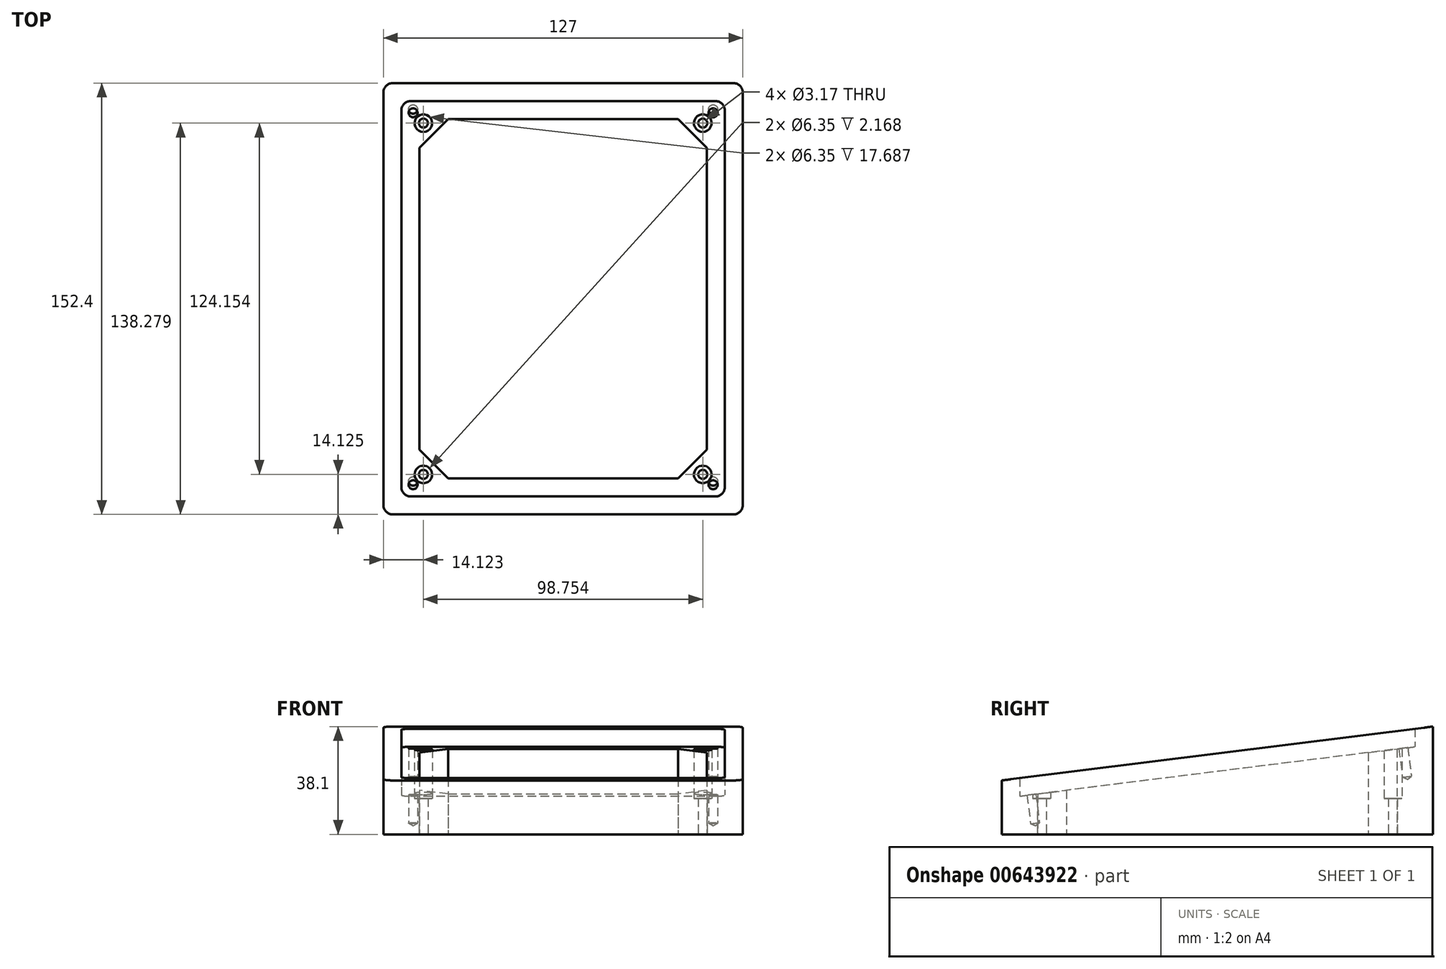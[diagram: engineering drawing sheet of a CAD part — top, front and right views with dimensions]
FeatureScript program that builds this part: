
annotation { "Feature Type Name" : "Feature", "Feature Type Description" : "" }
export const myFeature = defineFeature(function(context is Context, id is Id, definition is map)
    precondition{}
    {
        {
            var Q0;
            Q0=qCreatedBy(makeId("Top.planeOp"),FACE);
            var sketch = newSketch(context, id + "F0", { "sketchPlane" : qUnion([Q0])});
            skLineSegment(sketch, "E0.bottom", {"start": v(-63.5, 77.08) * mm, "end": v(63.5, 77.08) * mm});
            skLineSegment(sketch, "E0.top", {"start": v(-63.5, -75.32) * mm, "end": v(63.5, -75.32) * mm});
            skLineSegment(sketch, "E0.left", {"start": v(-63.5, 77.08) * mm, "end": v(-63.5, -75.32) * mm});
            skLineSegment(sketch, "E0.right", {"start": v(63.5, 77.08) * mm, "end": v(63.5, -75.32) * mm});
            skPoint(sketch, "E0.middle", {"position": v(0, 0.88) * mm});
            skLineSegment(sketch, "E1.bottom", {"start": v(-53.98, 70.73) * mm, "end": v(53.97, 70.73) * mm});
            skLineSegment(sketch, "E1.top", {"start": v(-53.98, -68.97) * mm, "end": v(53.97, -68.97) * mm});
            skLineSegment(sketch, "E1.left", {"start": v(-57.15, 67.56) * mm, "end": v(-57.15, -65.8) * mm});
            skLineSegment(sketch, "E1.right", {"start": v(57.15, 67.56) * mm, "end": v(57.15, -65.8) * mm});
            skLineSegment(sketch, "E2.bottom", {"start": v(-47.63, 64.38) * mm, "end": v(47.62, 64.38) * mm});
            skLineSegment(sketch, "E2.top", {"start": v(-47.63, -62.62) * mm, "end": v(48.25, -62.62) * mm});
            skLineSegment(sketch, "E2.left", {"start": v(-50.8, 61.2) * mm, "end": v(-50.8, -59.44) * mm});
            skLineSegment(sketch, "E2.right", {"start": v(50.8, 61.2) * mm, "end": v(50.8, -60.07) * mm});
            skPoint(sketch, "E3.visualSharp", {"position": v(-57.15, 70.73) * mm});
            skArc(sketch, "E3.filletArc", {"start": v(-53.98, 70.73) * mm, "mid": v(-56.22, 69.8) * mm, "end": v(-57.15, 67.56) * mm});
            skPoint(sketch, "E4.visualSharp", {"position": v(57.15, 70.73) * mm});
            skArc(sketch, "E4.filletArc", {"start": v(57.15, 67.56) * mm, "mid": v(56.22, 69.8) * mm, "end": v(53.97, 70.73) * mm});
            skPoint(sketch, "E5.visualSharp", {"position": v(57.15, -68.97) * mm});
            skArc(sketch, "E5.filletArc", {"start": v(53.97, -68.97) * mm, "mid": v(56.22, -68.04) * mm, "end": v(57.15, -65.8) * mm});
            skPoint(sketch, "E6.visualSharp", {"position": v(-57.15, -68.97) * mm});
            skArc(sketch, "E6.filletArc", {"start": v(-57.15, -65.8) * mm, "mid": v(-56.22, -68.04) * mm, "end": v(-53.98, -68.97) * mm});
            skPoint(sketch, "E7.visualSharp", {"position": v(50.8, 64.38) * mm});
            skArc(sketch, "E7.filletArc", {"start": v(50.8, 61.2) * mm, "mid": v(49.87, 63.45) * mm, "end": v(47.62, 64.38) * mm});
            skPoint(sketch, "E8.visualSharp", {"position": v(50.8, -62.62) * mm});
            skArc(sketch, "E8.filletArc", {"start": v(48.25, -62.62) * mm, "mid": v(50.05, -61.87) * mm, "end": v(50.8, -60.07) * mm});
            skPoint(sketch, "E9.visualSharp", {"position": v(-50.8, -62.62) * mm});
            skArc(sketch, "E9.filletArc", {"start": v(-50.8, -59.44) * mm, "mid": v(-49.87, -61.69) * mm, "end": v(-47.63, -62.62) * mm});
            skArc(sketch, "E10.filletArc", {"start": v(-47.63, 64.38) * mm, "mid": v(-49.87, 63.45) * mm, "end": v(-50.8, 61.2) * mm});
            skPoint(sketch, "E11.visualSharp", {"position": v(-63.5, 77.08) * mm});
            skLineSegment(sketch, "E11.filletArc", {"start": v(-63.5, 77.08) * mm, "end": v(-63.5, 77.08) * mm});
            skPoint(sketch, "E12.visualSharp", {"position": v(63.5, 77.08) * mm});
            skLineSegment(sketch, "E12.filletArc", {"start": v(63.5, 77.08) * mm, "end": v(63.5, 77.08) * mm});
            skPoint(sketch, "E13.visualSharp", {"position": v(63.5, -75.32) * mm});
            skLineSegment(sketch, "E13.filletArc", {"start": v(63.5, -75.32) * mm, "end": v(63.5, -75.32) * mm});
            skPoint(sketch, "E14.visualSharp", {"position": v(-63.5, -75.32) * mm});
            skLineSegment(sketch, "E14.filletArc", {"start": v(-63.5, -75.32) * mm, "end": v(-63.5, -75.32) * mm});
            skPoint(sketch, "E15", {"position": v(15.87, 64.38) * mm});
            skPoint(sketch, "E16", {"position": v(15.87, 77.08) * mm});
            skPoint(sketch, "E17", {"position": v(15.87, -62.62) * mm});
            skPoint(sketch, "E18", {"position": v(15.87, -75.32) * mm});
            skPoint(sketch, "E19", {"position": v(-15.88, 77.08) * mm});
            skPoint(sketch, "E20", {"position": v(-15.88, 64.38) * mm});
            skPoint(sketch, "E21", {"position": v(-15.88, -62.62) * mm});
            skPoint(sketch, "E22", {"position": v(-15.88, -75.32) * mm});
            skPoint(sketch, "E23", {"position": v(0, 77.08) * mm});
            skPoint(sketch, "E24", {"position": v(0, -75.32) * mm});
            skPoint(sketch, "E25", {"position": v(-63.5, 0.88) * mm});
            skPoint(sketch, "E26", {"position": v(63.5, 0.88) * mm});
            skPoint(sketch, "E27", {"position": v(63.5, 16.76) * mm});
            skPoint(sketch, "E28", {"position": v(50.8, 16.76) * mm});
            skPoint(sketch, "E29", {"position": v(-50.8, 16.76) * mm});
            skPoint(sketch, "E30", {"position": v(-63.5, 16.76) * mm});
            skPoint(sketch, "E31", {"position": v(63.5, -15) * mm});
            skPoint(sketch, "E32", {"position": v(50.8, -15) * mm});
            skPoint(sketch, "E33", {"position": v(-50.8, -15) * mm});
            skPoint(sketch, "E34", {"position": v(-63.5, -15) * mm});
            skPoint(sketch, "E35", {"position": v(40.64, 64.38) * mm});
            skPoint(sketch, "E36", {"position": v(40.64, -62.62) * mm});
            skPoint(sketch, "E37", {"position": v(-40.64, 64.38) * mm});
            skPoint(sketch, "E38", {"position": v(-40.64, -62.62) * mm});
            skPoint(sketch, "E39", {"position": v(-50.8, -52.46) * mm});
            skPoint(sketch, "E40", {"position": v(50.8, -52.46) * mm});
            skPoint(sketch, "E41", {"position": v(50.8, 54.22) * mm});
            skPoint(sketch, "E42", {"position": v(-50.8, 54.22) * mm});
            skLineSegment(sketch, "E43", {"start": v(-50.8, 54.22) * mm, "end": v(-40.64, 64.38) * mm});
            skLineSegment(sketch, "E44", {"start": v(40.64, 64.38) * mm, "end": v(50.8, 54.22) * mm});
            skLineSegment(sketch, "E45", {"start": v(50.8, -52.46) * mm, "end": v(40.64, -62.62) * mm});
            skLineSegment(sketch, "E46", {"start": v(-40.64, -62.62) * mm, "end": v(-50.8, -52.46) * mm});
            skPoint(sketch, "E47", {"position": v(-45.72, 59.3) * mm});
            skPoint(sketch, "E48", {"position": v(45.72, 59.3) * mm});
            skPoint(sketch, "E49", {"position": v(45.72, -57.54) * mm});
            skPoint(sketch, "E50", {"position": v(-45.72, -57.54) * mm});
            skPoint(sketch, "E51", {"position": v(30.16, 77.08) * mm});
            skPoint(sketch, "E52", {"position": v(30.16, 64.38) * mm});
            skPoint(sketch, "E53", {"position": v(30.16, -62.62) * mm});
            skPoint(sketch, "E54", {"position": v(30.16, -75.32) * mm});
            skPoint(sketch, "E55", {"position": v(-30.16, 77.08) * mm});
            skPoint(sketch, "E56", {"position": v(-30.16, 64.38) * mm});
            skPoint(sketch, "E57", {"position": v(-30.16, -62.62) * mm});
            skPoint(sketch, "E58", {"position": v(-30.16, -75.32) * mm});
            skPoint(sketch, "E59", {"position": v(63.5, 37.4) * mm});
            skPoint(sketch, "E60", {"position": v(50.8, 37.4) * mm});
            skPoint(sketch, "E61", {"position": v(-50.8, 37.4) * mm});
            skPoint(sketch, "E62", {"position": v(-63.5, 37.4) * mm});
            skPoint(sketch, "E63", {"position": v(63.5, -35.63) * mm});
            skPoint(sketch, "E64", {"position": v(50.8, -35.63) * mm});
            skPoint(sketch, "E65", {"position": v(-50.8, -35.63) * mm});
            skPoint(sketch, "E66", {"position": v(-63.5, -35.63) * mm});
            skPoint(sketch, "E67", {"position": v(-36.51, 77.08) * mm});
            skPoint(sketch, "E68", {"position": v(-36.51, 64.38) * mm});
            skPoint(sketch, "E69", {"position": v(-36.51, -62.62) * mm});
            skPoint(sketch, "E70", {"position": v(-36.51, -75.32) * mm});
            skPoint(sketch, "E71", {"position": v(36.51, 77.08) * mm});
            skPoint(sketch, "E72", {"position": v(36.51, 64.38) * mm});
            skPoint(sketch, "E73", {"position": v(36.51, -62.62) * mm});
            skPoint(sketch, "E74", {"position": v(36.51, -75.32) * mm});
            skPoint(sketch, "E75", {"position": v(-23.81, 77.08) * mm});
            skPoint(sketch, "E76", {"position": v(-23.81, 64.38) * mm});
            skPoint(sketch, "E77", {"position": v(23.81, 77.08) * mm});
            skPoint(sketch, "E78", {"position": v(23.81, 64.38) * mm});
            skPoint(sketch, "E79", {"position": v(23.81, -62.62) * mm});
            skPoint(sketch, "E80", {"position": v(23.81, -75.32) * mm});
            skPoint(sketch, "E81", {"position": v(-23.81, -62.62) * mm});
            skPoint(sketch, "E82", {"position": v(-23.81, -75.32) * mm});
            skPoint(sketch, "E83", {"position": v(-63.5, 43.74) * mm});
            skPoint(sketch, "E84", {"position": v(-50.8, 43.74) * mm});
            skPoint(sketch, "E85", {"position": v(50.8, 43.74) * mm});
            skPoint(sketch, "E86", {"position": v(63.5, 43.74) * mm});
            skPoint(sketch, "E87", {"position": v(-63.5, 31.04) * mm});
            skPoint(sketch, "E88", {"position": v(-50.8, 31.04) * mm});
            skPoint(sketch, "E89", {"position": v(50.8, 31.04) * mm});
            skPoint(sketch, "E90", {"position": v(63.5, 31.04) * mm});
            skPoint(sketch, "E91", {"position": v(-63.5, -29.28) * mm});
            skPoint(sketch, "E92", {"position": v(-50.8, -29.28) * mm});
            skPoint(sketch, "E93", {"position": v(50.8, -29.28) * mm});
            skPoint(sketch, "E94", {"position": v(63.5, -29.28) * mm});
            skPoint(sketch, "E95", {"position": v(-63.5, -41.98) * mm});
            skPoint(sketch, "E96", {"position": v(-50.8, -41.98) * mm});
            skPoint(sketch, "E97", {"position": v(50.8, -41.98) * mm});
            skPoint(sketch, "E98", {"position": v(63.5, -41.98) * mm});
            skLineSegment(sketch, "E99", {"start": v(57.15, 70.73) * mm, "end": v(45.72, 59.3) * mm, "construction": true});
            skLineSegment(sketch, "E100", {"start": v(57.15, -68.97) * mm, "end": v(45.72, -57.54) * mm, "construction": true});
            skLineSegment(sketch, "E101", {"start": v(-57.15, -68.97) * mm, "end": v(-45.72, -57.54) * mm, "construction": true});
            skPoint(sketch, "E102", {"position": v(53.04, 66.62) * mm});
            skLineSegment(sketch, "E103", {"start": v(-57.15, 70.73) * mm, "end": v(-45.72, 59.3) * mm, "construction": true});
            skPoint(sketch, "E104", {"position": v(-53.04, 66.62) * mm});
            skPoint(sketch, "E105", {"position": v(53.04, -64.86) * mm});
            skPoint(sketch, "E106", {"position": v(-53.04, -64.86) * mm});
            skCircle(sketch, "E107", {"center": v(-53.04, 66.62) * mm, "radius": 1.59 * mm});
            skCircle(sketch, "E108", {"center": v(53.04, 66.62) * mm, "radius": 1.59 * mm});
            skCircle(sketch, "E109", {"center": v(53.04, -64.86) * mm, "radius": 1.59 * mm});
            skCircle(sketch, "E110", {"center": v(-53.04, -64.86) * mm, "radius": 1.59 * mm});
            skPoint(sketch, "E111", {"position": v(-49.38, -61.2) * mm});
            skPoint(sketch, "E112", {"position": v(49.38, -61.2) * mm});
            skCircle(sketch, "E113", {"center": v(-49.38, -61.2) * mm, "radius": 1.59 * mm});
            skCircle(sketch, "E114", {"center": v(49.38, -61.2) * mm, "radius": 1.59 * mm});
            skPoint(sketch, "E115", {"position": v(-49.38, 62.96) * mm});
            skPoint(sketch, "E116", {"position": v(49.38, 62.96) * mm});
            skCircle(sketch, "E117", {"center": v(-49.38, 62.96) * mm, "radius": 1.59 * mm});
            skCircle(sketch, "E118", {"center": v(49.38, 62.96) * mm, "radius": 1.59 * mm});
            skCircle(sketch, "E119", {"center": v(-49.38, 62.96) * mm, "radius": 3.18 * mm});
            skCircle(sketch, "E120", {"center": v(49.38, 62.96) * mm, "radius": 3.18 * mm});
            skCircle(sketch, "E121", {"center": v(-49.38, -61.2) * mm, "radius": 3.18 * mm});
            skCircle(sketch, "E122", {"center": v(49.38, -61.2) * mm, "radius": 3.18 * mm});
            skSolve(sketch);
        }
        {
            var Q0;
            Q0=makeQuery(id+"F0.imprint","IMPRINT",FACE,{"disambiguationData":[TD([[makeQuery(id+"F0.imprint","IMPRINT",EDGE,{"derivedFrom":sQuery(id+"F0.wireOp",EDGE,"E0.bottom")}),-1.0]])]});
            var Q1;
            Q1=makeQuery(id+"F0.imprint","IMPRINT",FACE,{"disambiguationData":[TD([[makeQuery(id+"F0.imprint","IMPRINT",EDGE,{"derivedFrom":sQuery(id+"F0.wireOp",EDGE,"E1.bottom")}),-1.0]])]});
            var Q2;
            {var subQ5=sQuery(id+"F0.wireOp",EDGE,"E43");Q2=makeQuery(id+"F0.imprint","IMPRINT",FACE,{"disambiguationData":[TD([[makeQuery(id+"F0.imprint","IMPRINT",EDGE,{"derivedFrom":subQ5}),1.0]])]});}
            var Q3;
            {var subQ8=sQuery(id+"F0.wireOp",EDGE,"E44");Q3=makeQuery(id+"F0.imprint","IMPRINT",FACE,{"disambiguationData":[TD([[makeQuery(id+"F0.imprint","IMPRINT",EDGE,{"derivedFrom":subQ8}),1.0]])]});}
            var Q4;
            {var subQ8=sQuery(id+"F0.wireOp",EDGE,"E45");Q4=makeQuery(id+"F0.imprint","IMPRINT",FACE,{"disambiguationData":[TD([[makeQuery(id+"F0.imprint","IMPRINT",EDGE,{"derivedFrom":subQ8}),1.0]])]});}
            var Q5;
            {var subQ5=sQuery(id+"F0.wireOp",EDGE,"E46");Q5=makeQuery(id+"F0.imprint","IMPRINT",FACE,{"disambiguationData":[TD([[makeQuery(id+"F0.imprint","IMPRINT",EDGE,{"derivedFrom":subQ5}),1.0]])]});}
            var Q6;
            Q6=makeQuery(id+"F0.imprint","IMPRINT",FACE,{"disambiguationData":[TD([[makeQuery(id+"F0.imprint","IMPRINT",EDGE,{"derivedFrom":sQuery(id+"F0.wireOp",EDGE,"E108")}),1.0]])]});
            var Q7;
            Q7=makeQuery(id+"F0.imprint","IMPRINT",FACE,{"disambiguationData":[TD([[makeQuery(id+"F0.imprint","IMPRINT",EDGE,{"derivedFrom":sQuery(id+"F0.wireOp",EDGE,"E107")}),1.0]])]});
            var Q8;
            Q8=makeQuery(id+"F0.imprint","IMPRINT",FACE,{"disambiguationData":[TD([[makeQuery(id+"F0.imprint","IMPRINT",EDGE,{"derivedFrom":sQuery(id+"F0.wireOp",EDGE,"E109")}),1.0]])]});
            var Q9;
            Q9=makeQuery(id+"F0.imprint","IMPRINT",FACE,{"disambiguationData":[TD([[makeQuery(id+"F0.imprint","IMPRINT",EDGE,{"derivedFrom":sQuery(id+"F0.wireOp",EDGE,"E110")}),1.0]])]});
            extrude(context, id + "F1", {"entities" : qUnion([Q0, Q1, Q2, Q3, Q4, Q5, Q6, Q7, Q8, Q9]), "depth" : 76.2 * mm, "offsetDistance" : 25.4 * mm});
        }
        {
            var Q0;
            Q0=makeQuery(id+"F1.opExtrude","SWEPT_FACE",FACE,{"disambiguationData":[OSD([sQuery(id+"F0.wireOp",EDGE,"E0.right")])]});
            var sketch = newSketch(context, id + "F2", { "sketchPlane" : qUnion([Q0])});
            skPoint(sketch, "E123", {"position": v(77.08, 25.4) * mm});
            skPoint(sketch, "E124", {"position": v(77.08, 69.85) * mm});
            skPoint(sketch, "E125", {"position": v(-75.38, 25.4) * mm});
            skPoint(sketch, "E126", {"position": v(77.18, 69.85) * mm});
            skLineSegment(sketch, "E127", {"start": v(77.18, 82.96) * mm, "end": v(-75.38, 82.96) * mm});
            skPoint(sketch, "E128", {"position": v(-75.32, 19.05) * mm});
            skPoint(sketch, "E129", {"position": v(77.08, 38.1) * mm});
            skLineSegment(sketch, "E130", {"start": v(-75.32, 19.05) * mm, "end": v(77.08, 38.1) * mm});
            skLineSegment(sketch, "E131", {"start": v(-75.38, 82.96) * mm, "end": v(-75.32, 19.05) * mm});
            skLineSegment(sketch, "E132", {"start": v(77.18, 82.96) * mm, "end": v(77.08, 38.1) * mm});
            skSolve(sketch);
        }
        {
            var Q0;
            Q0=qSketchRegion(id+"F2",true);
            extrude(context, id + "F3", {"entities" : qUnion([Q0]), "operationType" : NewBodyOperationType.REMOVE, "oppositeDirection" : true, "depth" : 133.86 * mm, "offsetDistance" : 25.4 * mm});
        }
        {
            var Q0;
            {var subQ0=sQuery(id+"F0.wireOp",EDGE,"E10.filletArc");var subQ1=sQuery(id+"F0.wireOp",EDGE,"E2.bottom");var subQ2=makeQuery(id+"F0.imprint","INTERSECT",VERTEX,{"derivedFrom":[subQ1,subQ0]});Q0=makeQuery(id+"F0.imprint","IMPRINT",FACE,{"disambiguationData":[TD([[makeQuery(id+"F0.imprint","IMPRINT",EDGE,{"disambiguationData":[TD([[subQ2,-1.0]])],"derivedFrom":subQ1}),-1.0]])]});}
            var Q1;
            {var subQ0=sQuery(id+"F0.wireOp",EDGE,"E10.filletArc");var subQ1=sQuery(id+"F0.wireOp",EDGE,"E2.bottom");var subQ2=makeQuery(id+"F0.imprint","INTERSECT",VERTEX,{"derivedFrom":[subQ1,subQ0]});Q1=makeQuery(id+"F0.imprint","IMPRINT",FACE,{"disambiguationData":[TD([[makeQuery(id+"F0.imprint","IMPRINT",EDGE,{"disambiguationData":[TD([[subQ2,-1.0]])],"derivedFrom":subQ1}),1.0]])]});}
            var Q2;
            {var subQ0=sQuery(id+"F0.wireOp",EDGE,"E7.filletArc");var subQ1=sQuery(id+"F0.wireOp",EDGE,"E2.bottom");var subQ2=makeQuery(id+"F0.imprint","INTERSECT",VERTEX,{"derivedFrom":[subQ1,subQ0]});Q2=makeQuery(id+"F0.imprint","IMPRINT",FACE,{"disambiguationData":[TD([[makeQuery(id+"F0.imprint","IMPRINT",EDGE,{"disambiguationData":[TD([[subQ2,1.0]])],"derivedFrom":subQ1}),-1.0]])]});}
            var Q3;
            {var subQ0=sQuery(id+"F0.wireOp",EDGE,"E7.filletArc");var subQ1=sQuery(id+"F0.wireOp",EDGE,"E2.bottom");var subQ2=makeQuery(id+"F0.imprint","INTERSECT",VERTEX,{"derivedFrom":[subQ1,subQ0]});Q3=makeQuery(id+"F0.imprint","IMPRINT",FACE,{"disambiguationData":[TD([[makeQuery(id+"F0.imprint","IMPRINT",EDGE,{"disambiguationData":[TD([[subQ2,1.0]])],"derivedFrom":subQ1}),1.0]])]});}
            var Q4;
            {var subQ0=sQuery(id+"F0.wireOp",EDGE,"E8.filletArc");var subQ1=sQuery(id+"F0.wireOp",EDGE,"E2.top");var subQ2=makeQuery(id+"F0.imprint","INTERSECT",VERTEX,{"derivedFrom":[subQ1,subQ0]});Q4=makeQuery(id+"F0.imprint","IMPRINT",FACE,{"disambiguationData":[TD([[makeQuery(id+"F0.imprint","IMPRINT",EDGE,{"disambiguationData":[TD([[subQ2,1.0]])],"derivedFrom":subQ1}),-1.0]])]});}
            var Q5;
            {var subQ0=sQuery(id+"F0.wireOp",EDGE,"E8.filletArc");var subQ1=sQuery(id+"F0.wireOp",EDGE,"E2.top");var subQ2=makeQuery(id+"F0.imprint","INTERSECT",VERTEX,{"derivedFrom":[subQ1,subQ0]});Q5=makeQuery(id+"F0.imprint","IMPRINT",FACE,{"disambiguationData":[TD([[makeQuery(id+"F0.imprint","IMPRINT",EDGE,{"disambiguationData":[TD([[subQ2,1.0]])],"derivedFrom":subQ1}),1.0]])]});}
            var Q6;
            {var subQ0=sQuery(id+"F0.wireOp",EDGE,"E9.filletArc");var subQ1=sQuery(id+"F0.wireOp",EDGE,"E2.top");var subQ2=makeQuery(id+"F0.imprint","INTERSECT",VERTEX,{"derivedFrom":[subQ1,subQ0]});Q6=makeQuery(id+"F0.imprint","IMPRINT",FACE,{"disambiguationData":[TD([[makeQuery(id+"F0.imprint","IMPRINT",EDGE,{"disambiguationData":[TD([[subQ2,-1.0]])],"derivedFrom":subQ1}),-1.0]])]});}
            var Q7;
            {var subQ0=sQuery(id+"F0.wireOp",EDGE,"E9.filletArc");var subQ1=sQuery(id+"F0.wireOp",EDGE,"E2.top");var subQ2=makeQuery(id+"F0.imprint","INTERSECT",VERTEX,{"derivedFrom":[subQ1,subQ0]});Q7=makeQuery(id+"F0.imprint","IMPRINT",FACE,{"disambiguationData":[TD([[makeQuery(id+"F0.imprint","IMPRINT",EDGE,{"disambiguationData":[TD([[subQ2,-1.0]])],"derivedFrom":subQ1}),1.0]])]});}
            extrude(context, id + "F4", {"entities" : qUnion([Q0, Q1, Q2, Q3, Q4, Q5, Q6, Q7]), "operationType" : NewBodyOperationType.ADD, "depth" : 12.7 * mm, "offsetDistance" : 25.4 * mm});
        }
        {
            var Q0;
            Q0=makeQuery(id+"F1.opExtrude","SWEPT_FACE",FACE,{"disambiguationData":[OSD([sQuery(id+"F0.wireOp",EDGE,"E0.right")])]});
            var sketch = newSketch(context, id + "F5", { "sketchPlane" : qUnion([Q0])});
            skPoint(sketch, "E133", {"position": v(-75.32, 12.7) * mm});
            skPoint(sketch, "E134", {"position": v(77.08, 31.75) * mm});
            skPoint(sketch, "E135", {"position": v(-68.97, 0) * mm});
            skPoint(sketch, "E136", {"position": v(70.73, 0) * mm});
            skPoint(sketch, "E137", {"position": v(-68.97, 13.5) * mm});
            skPoint(sketch, "E138", {"position": v(-68.97, 19.84) * mm});
            skPoint(sketch, "E139", {"position": v(70.73, 30.96) * mm});
            skPoint(sketch, "E140", {"position": v(70.73, 37.3) * mm});
            skLineSegment(sketch, "E141", {"start": v(-68.97, 19.84) * mm, "end": v(-68.97, 13.5) * mm});
            skLineSegment(sketch, "E142", {"start": v(70.73, 37.3) * mm, "end": v(70.73, 30.96) * mm});
            skLineSegment(sketch, "E143", {"start": v(70.73, 30.96) * mm, "end": v(-68.97, 13.5) * mm});
            skLineSegment(sketch, "E144", {"start": v(-68.97, 19.84) * mm, "end": v(70.73, 37.3) * mm});
            skPoint(sketch, "E145", {"position": v(70.73, 13.5) * mm});
            skLineSegment(sketch, "E146", {"start": v(-68.97, 13.5) * mm, "end": v(70.73, 13.5) * mm, "construction": true});
            skLineSegment(sketch, "E147", {"start": v(70.73, 30.96) * mm, "end": v(70.73, 13.5) * mm, "construction": true});
            skSolve(sketch);
        }
        {
            var Q0;
            Q0=makeQuery(id+"F5.imprint","IMPRINT",FACE,{"disambiguationData":[TD([[makeQuery(id+"F5.imprint","IMPRINT",EDGE,{"derivedFrom":sQuery(id+"F5.wireOp",EDGE,"E141")}),1.0]])]});
            extrude(context, id + "F6", {"entities" : qUnion([Q0]), "operationType" : NewBodyOperationType.REMOVE, "oppositeDirection" : true, "depth" : 120.65 * mm, "offsetDistance" : 25.4 * mm, "hasSecondDirection" : true, "secondDirectionOppositeDirection" : true, "secondDirectionDepth" : 6.35 * mm});
        }
        {
            var Q0;
            Q0=makeQuery(id+"F6.boolean.opBoolean","COPY",FACE,{"derivedFrom":makeQuery(id+"F6.opExtrude","SWEPT_FACE",FACE,{"disambiguationData":[OSD([sQuery(id+"F5.wireOp",EDGE,"E143")])]})});
            var sketch = newSketch(context, id + "F7", { "sketchPlane" : qUnion([Q0])});
            skPoint(sketch, "E148", {"position": v(-57.15, 74.03) * mm});
            skPoint(sketch, "E149", {"position": v(-49.38, 66.2) * mm});
            skPoint(sketch, "E150", {"position": v(49.38, 66.2) * mm});
            skPoint(sketch, "E151", {"position": v(57.15, 74.03) * mm});
            skPoint(sketch, "E152", {"position": v(49.38, -58.93) * mm});
            skPoint(sketch, "E153", {"position": v(57.15, -66.76) * mm});
            skPoint(sketch, "E154", {"position": v(-49.38, -58.93) * mm});
            skPoint(sketch, "E155", {"position": v(-57.15, -66.76) * mm});
            skLineSegment(sketch, "E156", {"start": v(-49.38, -58.93) * mm, "end": v(-57.15, -66.76) * mm, "construction": true});
            skLineSegment(sketch, "E157", {"start": v(49.38, -58.93) * mm, "end": v(57.15, -66.76) * mm, "construction": true});
            skLineSegment(sketch, "E158", {"start": v(57.15, 74.03) * mm, "end": v(49.38, 66.2) * mm, "construction": true});
            skLineSegment(sketch, "E159", {"start": v(-57.15, 74.03) * mm, "end": v(-49.38, 66.2) * mm, "construction": true});
            skPoint(sketch, "E160", {"position": v(-53.04, 69.88) * mm});
            skPoint(sketch, "E161", {"position": v(53.04, 69.88) * mm});
            skPoint(sketch, "E162", {"position": v(53.04, -62.61) * mm});
            skPoint(sketch, "E163", {"position": v(-53.04, -62.61) * mm});
            skSolve(sketch);
        }
        {
            var Q0;
            Q0=sQuery(id+"F7.wireOp",VERTEX,"E160");
            var Q1;
            Q1=sQuery(id+"F7.wireOp",VERTEX,"E161");
            var Q2;
            Q2=sQuery(id+"F7.wireOp",VERTEX,"E162");
            var Q3;
            Q3=sQuery(id+"F7.wireOp",VERTEX,"E163");
            var Q4;
            Q4=makeQuery(id+"F1.opExtrude","SWEPT_BODY",BODY,{"disambiguationData":[OSD([sQuery(id+"F0.wireOp",EDGE,"E0.bottom"),sQuery(id+"F0.wireOp",EDGE,"E0.top"),sQuery(id+"F0.wireOp",EDGE,"E0.left"),sQuery(id+"F0.wireOp",EDGE,"E0.right"),sQuery(id+"F0.wireOp",EDGE,"E2.bottom"),sQuery(id+"F0.wireOp",EDGE,"E2.top"),sQuery(id+"F0.wireOp",EDGE,"E2.left"),sQuery(id+"F0.wireOp",EDGE,"E2.right"),sQuery(id+"F0.wireOp",EDGE,"E43"),sQuery(id+"F0.wireOp",EDGE,"E44"),sQuery(id+"F0.wireOp",EDGE,"E45"),sQuery(id+"F0.wireOp",EDGE,"E46"),sQuery(id+"F0.wireOp",EDGE,"E119"),sQuery(id+"F0.wireOp",EDGE,"E120"),sQuery(id+"F0.wireOp",EDGE,"E121"),sQuery(id+"F0.wireOp",EDGE,"E122")])]});
            hole(context, id + "F8", {"style" : HoleStyle.SIMPLE, "endStyle" : HoleEndStyle.BLIND, "holeDiameter" : 3.17 * mm, "majorDiameter" : 6.35 * mm, "holeDepth" : 10.16 * mm, "isTappedThrough" : true, "tappedDepth" : 12.7 * mm, "tapClearance" : 3, "locations" : qUnion([Q0, Q1, Q2, Q3]), "scope" : qUnion([Q4])});
        }
        {
            var Q0;
            Q0=makeQuery(id+"F1.opExtrude","SWEPT_EDGE",EDGE,{"disambiguationData":[OSD([sQuery(id+"F0.wireOp",EDGE,"E0.bottom"),sQuery(id+"F0.wireOp",EDGE,"E0.right")])]});
            var Q1;
            Q1=makeQuery(id+"F1.opExtrude","SWEPT_EDGE",EDGE,{"disambiguationData":[OSD([sQuery(id+"F0.wireOp",EDGE,"E0.bottom"),sQuery(id+"F0.wireOp",EDGE,"E0.left")])]});
            var Q2;
            Q2=makeQuery(id+"F1.opExtrude","SWEPT_EDGE",EDGE,{"disambiguationData":[OSD([sQuery(id+"F0.wireOp",EDGE,"E0.top"),sQuery(id+"F0.wireOp",EDGE,"E0.right")])]});
            var Q3;
            Q3=makeQuery(id+"F1.opExtrude","SWEPT_EDGE",EDGE,{"disambiguationData":[OSD([sQuery(id+"F0.wireOp",EDGE,"E0.top"),sQuery(id+"F0.wireOp",EDGE,"E0.left")])]});
            var Q4;
            Q4=makeQuery(id+"F6.boolean.opBoolean","COPY",EDGE,{"derivedFrom":makeQuery(id+"F6.opExtrude","CAP_EDGE",EDGE,{"disambiguationData":[OSD([sQuery(id+"F5.wireOp",EDGE,"E142")])],"isStart":false})});
            var Q5;
            Q5=makeQuery(id+"F6.boolean.opBoolean","COPY",EDGE,{"derivedFrom":makeQuery(id+"F6.opExtrude","CAP_EDGE",EDGE,{"disambiguationData":[OSD([sQuery(id+"F5.wireOp",EDGE,"E142")])],"isStart":true})});
            var Q6;
            Q6=makeQuery(id+"F6.boolean.opBoolean","COPY",EDGE,{"derivedFrom":makeQuery(id+"F6.opExtrude","CAP_EDGE",EDGE,{"disambiguationData":[OSD([sQuery(id+"F5.wireOp",EDGE,"E141")])],"isStart":false})});
            var Q7;
            Q7=makeQuery(id+"F6.boolean.opBoolean","COPY",EDGE,{"derivedFrom":makeQuery(id+"F6.opExtrude","CAP_EDGE",EDGE,{"disambiguationData":[OSD([sQuery(id+"F5.wireOp",EDGE,"E141")])],"isStart":true})});
            fillet(context, id + "F9", {"entities" : qUnion([Q0, Q1, Q2, Q3, Q4, Q5, Q6, Q7]), "radius" : 3.17 * mm, "tangentPropagation" : true, "allowEdgeOverflow" : false});
        }
    });
